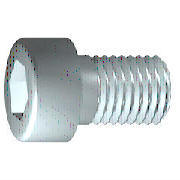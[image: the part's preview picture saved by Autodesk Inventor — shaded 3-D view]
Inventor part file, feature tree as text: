
AUTODESK INVENTOR PART (.ipt)
format: ipt  version: 2013 (Build 170138000, 138)  size: 178,688 bytes
history: native  units: mm (DEFAULTED — no unit token found)
features: sketch x2, extrude x1, plane x1, fillet x1
ambient origin geometry x7: Origin, YZ Plane, XY Plane, X Axis, Y Axis, Z Axis, Center Point
bodies: Solid1 (feature_tree), Body (feature_tree)
feature tree (5):
  extrude  "Slot"  Depth=0.766912mm
  plane  "Work Plane1"
  fillet  "Fillet2"  Radius=8.0mm
  sketch  "Sketch1"  dims[d1=28.0mm d2=0.766912mm d3=8.0mm]
  sketch  "Sketch2"  dims[d4=4.0mm d5=60.0deg d6=8.0mm d7=8.0mm d8=6.928203mm d9=13.0mm d10=90.0deg d11=10.0mm d12=0.0mm d13=28.0mm d14=0.0mm d15=0.766812mm d16=0.766813mm d17=0.8mm d19=0.0mm d26=120.0mm d27=45.0deg d28=0.0mm d29=0.0mm d30=0.1mm]
